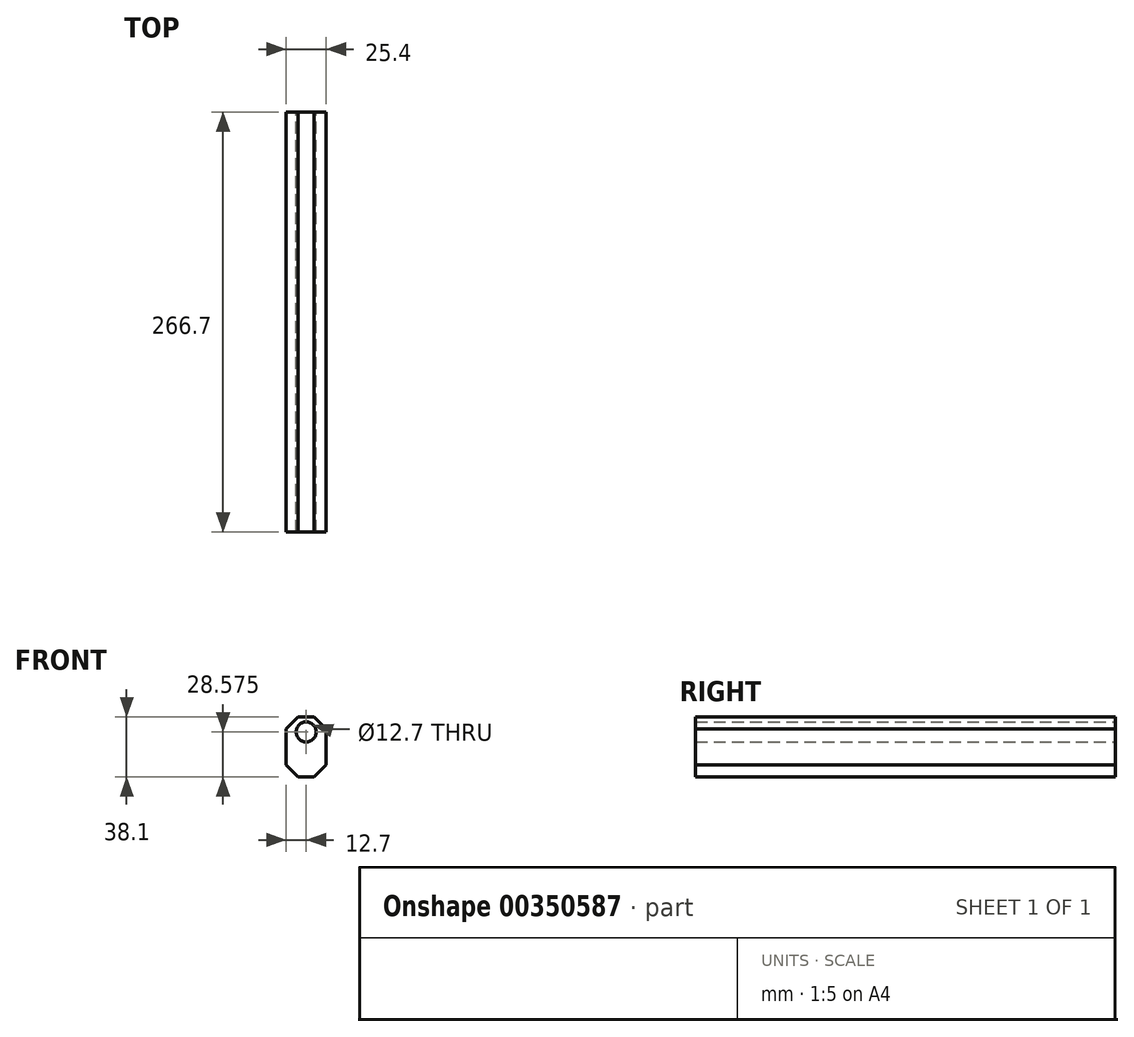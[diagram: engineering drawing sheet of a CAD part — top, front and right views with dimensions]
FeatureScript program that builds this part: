
annotation { "Feature Type Name" : "Feature", "Feature Type Description" : "" }
export const myFeature = defineFeature(function(context is Context, id is Id, definition is map)
    precondition{}
    {
        {
            var Q0;
            Q0=qCreatedBy(makeId("Front.planeOp"),FACE);
            var sketch = newSketch(context, id + "F0", { "sketchPlane" : qUnion([Q0])});
            skLineSegment(sketch, "E0.bottom", {"start": v(-12.7, 19.05) * mm, "end": v(12.7, 19.05) * mm});
            skLineSegment(sketch, "E0.top", {"start": v(-12.7, -19.05) * mm, "end": v(12.7, -19.05) * mm});
            skLineSegment(sketch, "E0.left", {"start": v(-12.7, 19.05) * mm, "end": v(-12.7, -19.05) * mm});
            skLineSegment(sketch, "E0.right", {"start": v(12.7, 19.05) * mm, "end": v(12.7, -19.05) * mm});
            skPoint(sketch, "E0.middle", {"position": v(0, 0) * mm});
            skCircle(sketch, "E1", {"center": v(0, 9.53) * mm, "radius": 6.35 * mm});
            skSolve(sketch);
        }
        {
            var Q0;
            Q0=makeQuery(id+"F0.imprint","IMPRINT",FACE,{"disambiguationData":[TD([[makeQuery(id+"F0.imprint","IMPRINT",EDGE,{"derivedFrom":sQuery(id+"F0.wireOp",EDGE,"E0.bottom")}),-1.0]])]});
            extrude(context, id + "F1", {"entities" : qUnion([Q0]), "endBound" : BoundingType.SYMMETRIC, "depth" : 266.7 * mm});
        }
        {
            var Q0;
            Q0=makeQuery(id+"F1.opExtrude","SWEPT_EDGE",EDGE,{"disambiguationData":[OSD([sQuery(id+"F0.wireOp",EDGE,"E0.bottom"),sQuery(id+"F0.wireOp",EDGE,"E0.right")])]});
            chamfer(context, id + "F2", {"entities" : qUnion([Q0]), "width" : 7.62 * mm, "tangentPropagation" : true});
        }
        {
            var Q0;
            Q0=makeQuery(id+"F1.opExtrude","SWEPT_EDGE",EDGE,{"disambiguationData":[OSD([sQuery(id+"F0.wireOp",EDGE,"E0.bottom"),sQuery(id+"F0.wireOp",EDGE,"E0.left")])]});
            chamfer(context, id + "F3", {"entities" : qUnion([Q0]), "width" : 7.62 * mm, "tangentPropagation" : true});
        }
        {
            var Q0;
            Q0=makeQuery(id+"F1.opExtrude","SWEPT_EDGE",EDGE,{"disambiguationData":[OSD([sQuery(id+"F0.wireOp",EDGE,"E0.top"),sQuery(id+"F0.wireOp",EDGE,"E0.left")])]});
            chamfer(context, id + "F4", {"entities" : qUnion([Q0]), "width" : 7.62 * mm, "tangentPropagation" : true});
        }
        {
            var Q0;
            Q0=makeQuery(id+"F1.opExtrude","SWEPT_EDGE",EDGE,{"disambiguationData":[OSD([sQuery(id+"F0.wireOp",EDGE,"E0.top"),sQuery(id+"F0.wireOp",EDGE,"E0.right")])]});
            chamfer(context, id + "F5", {"entities" : qUnion([Q0]), "width" : 7.62 * mm, "tangentPropagation" : true});
        }
    });
